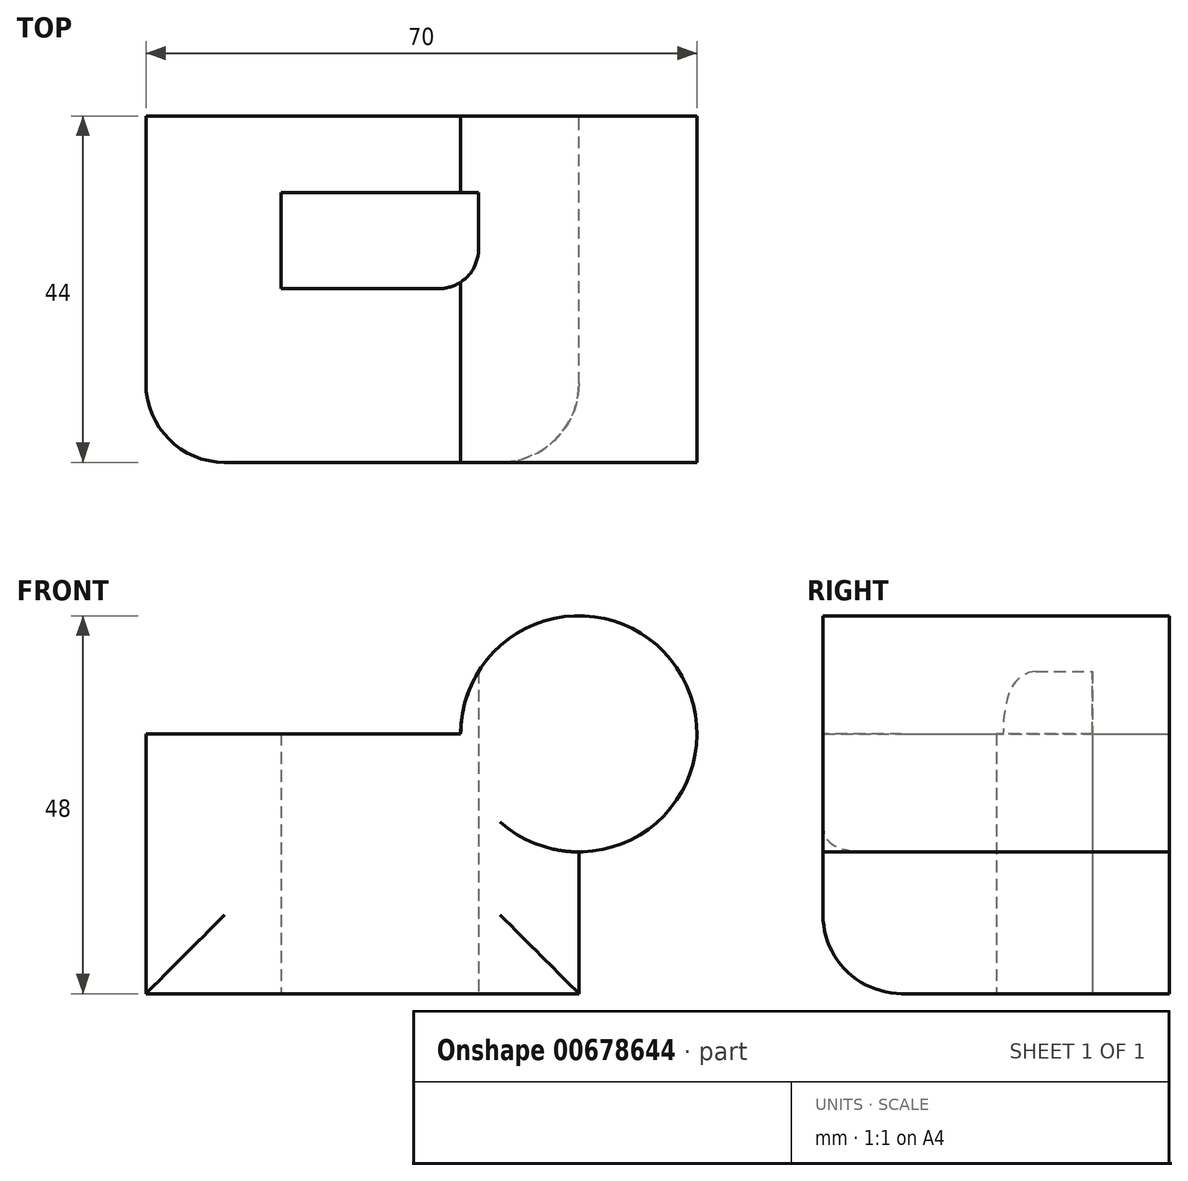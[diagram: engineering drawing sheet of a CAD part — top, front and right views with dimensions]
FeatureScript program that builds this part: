
annotation { "Feature Type Name" : "Feature", "Feature Type Description" : "" }
export const myFeature = defineFeature(function(context is Context, id is Id, definition is map)
    precondition{}
    {
        {
            var Q0;
            Q0=qCreatedBy(makeId("Front.planeOp"),FACE);
            var sketch = newSketch(context, id + "F0", { "sketchPlane" : qUnion([Q0])});
            skLineSegment(sketch, "E0.bottom", {"start": v(-22, 7.33) * mm, "end": v(18, 7.33) * mm});
            skLineSegment(sketch, "E0.top", {"start": v(-22, -25.67) * mm, "end": v(33, -25.67) * mm});
            skLineSegment(sketch, "E0.left", {"start": v(-22, 7.33) * mm, "end": v(-22, -25.67) * mm});
            skLineSegment(sketch, "E0.right", {"start": v(33, -7.67) * mm, "end": v(33, -25.67) * mm});
            skArc(sketch, "E1", {"start": v(33, -7.67) * mm, "mid": v(43.6, 17.94) * mm, "end": v(18, 7.33) * mm});
            skSolve(sketch);
        }
        {
            var Q0;
            Q0=makeQuery(id+"F0.imprint","IMPRINT",FACE,{"disambiguationData":[TD([[makeQuery(id+"F0.imprint","IMPRINT",EDGE,{"derivedFrom":sQuery(id+"F0.wireOp",EDGE,"E0.bottom")}),-1.0]])]});
            extrude(context, id + "F1", {"entities" : qUnion([Q0]), "depth" : 44 * mm, "offsetDistance" : 25 * mm});
        }
        {
            var Q0;
            Q0=makeQuery(id+"F1.opExtrude","CAP_EDGE",EDGE,{"disambiguationData":[OSD([sQuery(id+"F0.wireOp",EDGE,"E0.top")])],"isStart":false});
            var Q1;
            Q1=makeQuery(id+"F1.opExtrude","CAP_EDGE",EDGE,{"disambiguationData":[OSD([sQuery(id+"F0.wireOp",EDGE,"E0.right")])],"isStart":false});
            var Q2;
            Q2=makeQuery(id+"F1.opExtrude","CAP_EDGE",EDGE,{"disambiguationData":[OSD([sQuery(id+"F0.wireOp",EDGE,"E0.left")])],"isStart":false});
            fillet(context, id + "F2", {"entities" : qUnion([Q0, Q1, Q2]), "radius" : 10 * mm, "tangentPropagation" : true, "allowEdgeOverflow" : false});
        }
        {
            var Q0;
            Q0=makeQuery(id+"F1.opExtrude","SWEPT_FACE",FACE,{"disambiguationData":[OSD([sQuery(id+"F0.wireOp",EDGE,"E0.top")])]});
            var sketch = newSketch(context, id + "F3", { "sketchPlane" : qUnion([Q0])});
            skLineSegment(sketch, "E2.bottom", {"start": v(-4.8, 21.93) * mm, "end": v(15.25, 21.93) * mm});
            skLineSegment(sketch, "E2.top", {"start": v(-4.8, 9.75) * mm, "end": v(20.25, 9.75) * mm});
            skLineSegment(sketch, "E2.left", {"start": v(-4.8, 21.93) * mm, "end": v(-4.8, 9.75) * mm});
            skLineSegment(sketch, "E2.right", {"start": v(20.25, 16.93) * mm, "end": v(20.25, 9.75) * mm});
            skPoint(sketch, "E3.visualSharp", {"position": v(20.25, 21.93) * mm});
            skArc(sketch, "E3.filletArc", {"start": v(20.25, 16.93) * mm, "mid": v(18.79, 20.46) * mm, "end": v(15.25, 21.93) * mm});
            skSolve(sketch);
        }
        {
            var Q0;
            Q0=makeQuery(id+"F3.imprint","IMPRINT",FACE,{"disambiguationData":[TD([[makeQuery(id+"F3.imprint","IMPRINT",EDGE,{"derivedFrom":sQuery(id+"F3.wireOp",EDGE,"E2.bottom")}),-1.0]])]});
            extrude(context, id + "F4", {"entities" : qUnion([Q0]), "operationType" : NewBodyOperationType.REMOVE, "oppositeDirection" : true, "depth" : 50.9 * mm, "offsetDistance" : 25 * mm});
        }
    });
